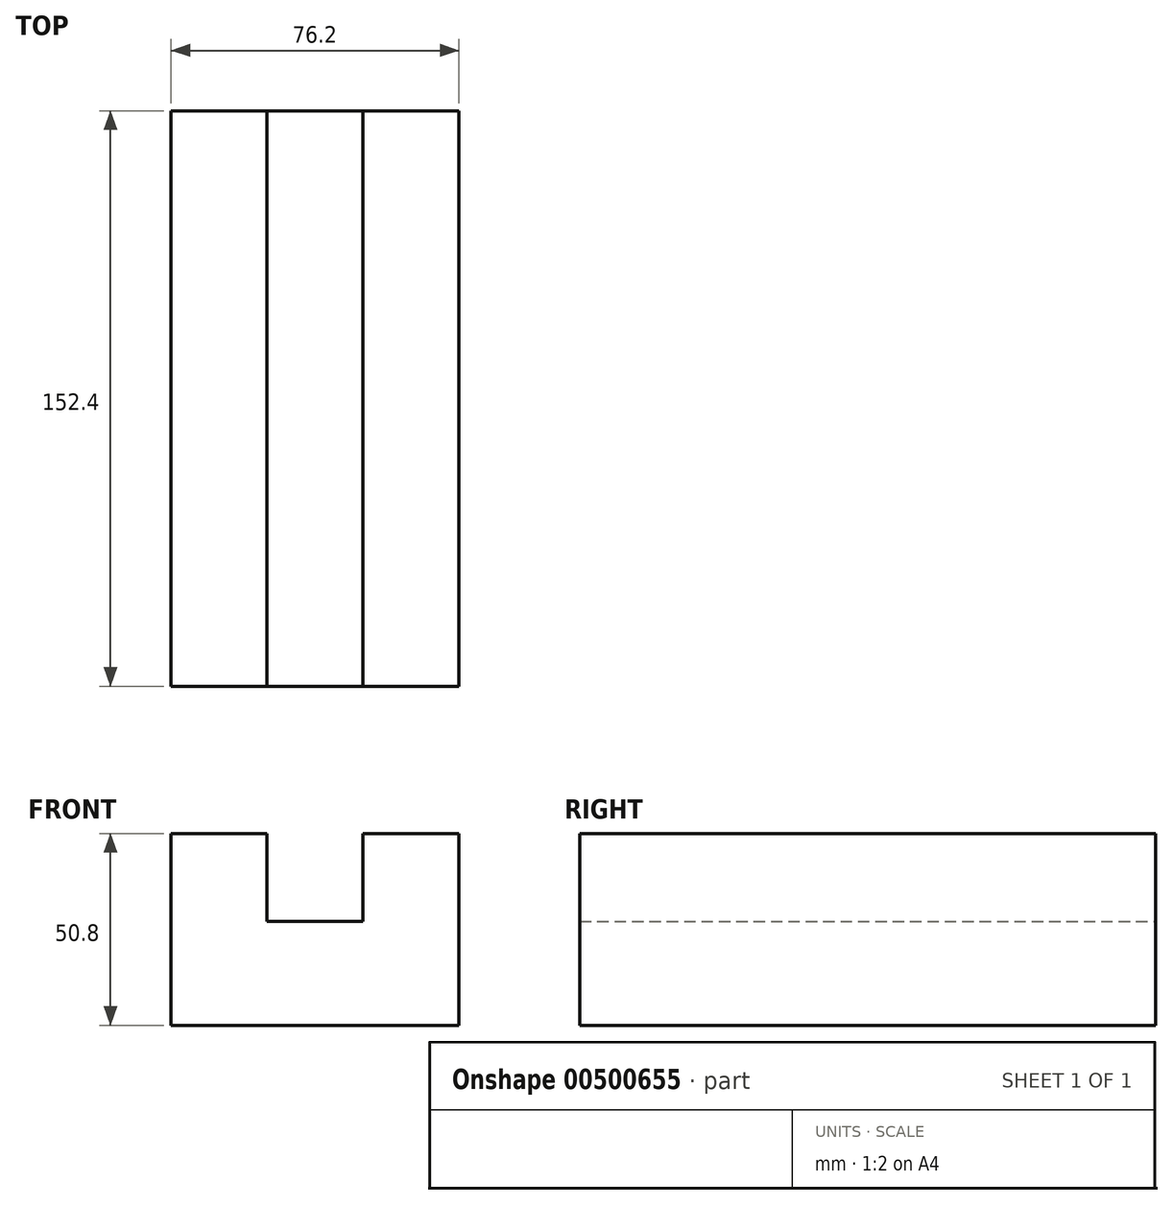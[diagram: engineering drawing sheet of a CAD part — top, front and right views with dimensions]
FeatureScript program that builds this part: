
annotation { "Feature Type Name" : "Feature", "Feature Type Description" : "" }
export const myFeature = defineFeature(function(context is Context, id is Id, definition is map)
    precondition{}
    {
        {
            var Q0;
            Q0=qCreatedBy(makeId("Front.planeOp"),FACE);
            var sketch = newSketch(context, id + "F0", { "sketchPlane" : qUnion([Q0])});
            skLineSegment(sketch, "E0", {"start": v(-31, 36.09) * mm, "end": v(-5.6, 36.09) * mm});
            skLineSegment(sketch, "E1", {"start": v(-5.6, 36.09) * mm, "end": v(-5.6, 12.83) * mm});
            skLineSegment(sketch, "E2", {"start": v(-5.6, 12.83) * mm, "end": v(19.8, 12.83) * mm});
            skLineSegment(sketch, "E3", {"start": v(19.8, 12.83) * mm, "end": v(19.8, 36.09) * mm});
            skLineSegment(sketch, "E4", {"start": v(19.8, 36.09) * mm, "end": v(45.2, 36.09) * mm});
            skLineSegment(sketch, "E5", {"start": v(45.2, 36.09) * mm, "end": v(45.2, -14.71) * mm});
            skLineSegment(sketch, "E6", {"start": v(45.2, -14.71) * mm, "end": v(-31, -14.71) * mm});
            skLineSegment(sketch, "E7", {"start": v(-31, -14.71) * mm, "end": v(-31, 36.09) * mm});
            skSolve(sketch);
        }
        {
            var Q0;
            Q0=makeQuery(id+"F0.imprint","IMPRINT",FACE,{"disambiguationData":[TD([[makeQuery(id+"F0.imprint","IMPRINT",EDGE,{"derivedFrom":sQuery(id+"F0.wireOp",EDGE,"E0")}),-1.0]])]});
            extrude(context, id + "F1", {"entities" : qUnion([Q0]), "depth" : 152.4 * mm});
        }
    });
